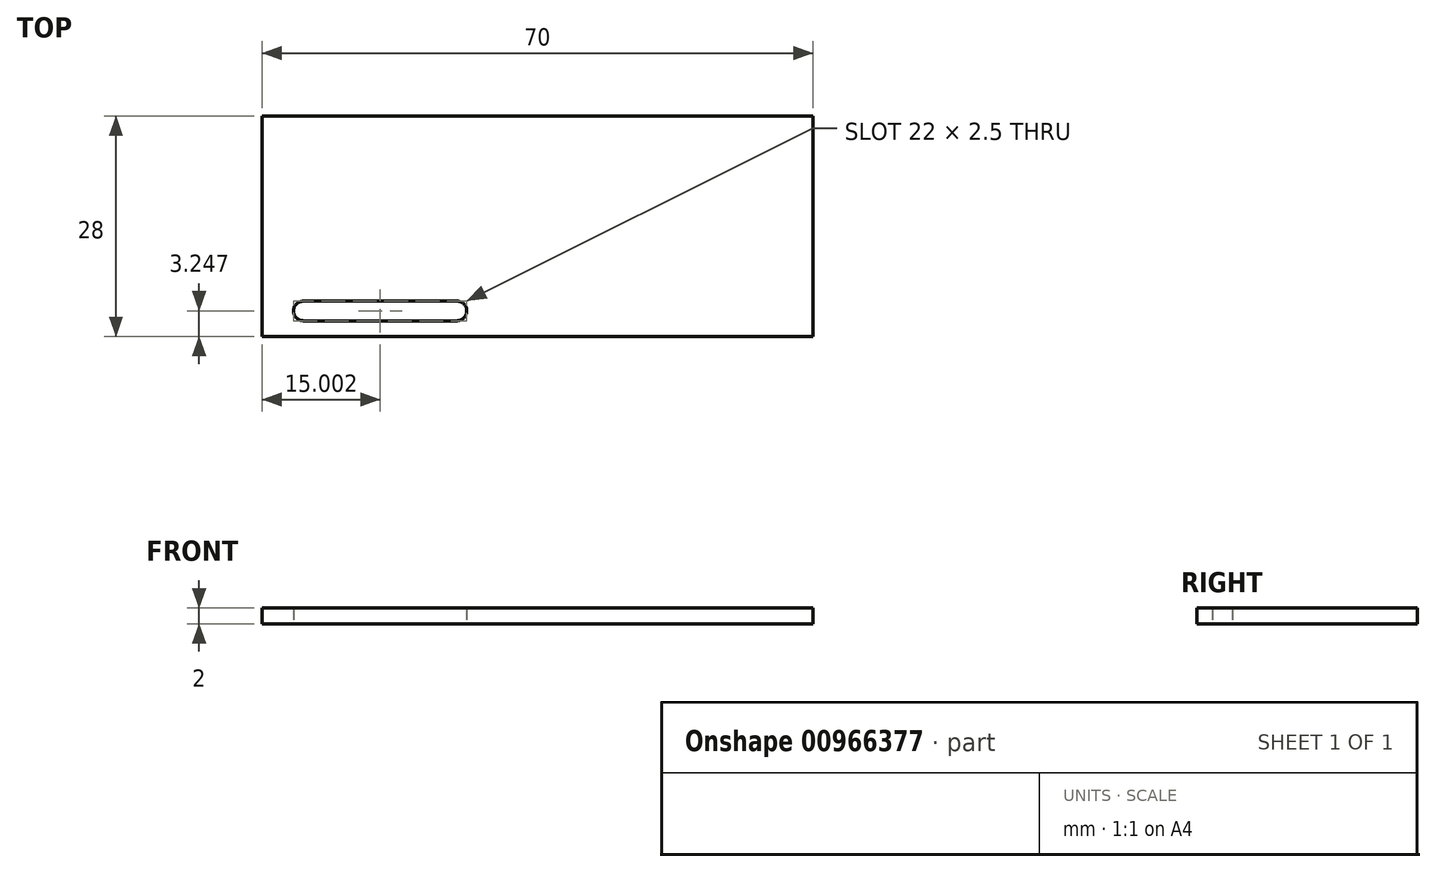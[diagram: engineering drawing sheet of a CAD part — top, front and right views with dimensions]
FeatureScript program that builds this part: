
annotation { "Feature Type Name" : "Feature", "Feature Type Description" : "" }
export const myFeature = defineFeature(function(context is Context, id is Id, definition is map)
    precondition{}
    {
        {
            var Q0;
            Q0=qCreatedBy(makeId("Top.planeOp"),FACE);
            var sketch = newSketch(context, id + "F0", { "sketchPlane" : qUnion([Q0])});
            skLineSegment(sketch, "E0.bottom", {"start": v(-29.62, 6.19) * mm, "end": v(40.38, 6.19) * mm});
            skLineSegment(sketch, "E0.top", {"start": v(-29.62, -21.81) * mm, "end": v(40.38, -21.81) * mm});
            skLineSegment(sketch, "E0.left", {"start": v(-29.62, 6.19) * mm, "end": v(-29.62, -21.81) * mm});
            skLineSegment(sketch, "E0.right", {"start": v(40.38, 6.19) * mm, "end": v(40.38, -21.81) * mm});
            skArc(sketch, "E1", {"start": v(-24.37, -17.31) * mm, "mid": v(-25.62, -18.56) * mm, "end": v(-24.37, -19.81) * mm});
            skArc(sketch, "E2", {"start": v(-4.87, -19.81) * mm, "mid": v(-3.62, -18.56) * mm, "end": v(-4.87, -17.31) * mm});
            skLineSegment(sketch, "E3", {"start": v(-24.37, -17.31) * mm, "end": v(-4.87, -17.31) * mm});
            skLineSegment(sketch, "E4", {"start": v(-24.37, -19.81) * mm, "end": v(-4.87, -19.81) * mm});
            skSolve(sketch);
        }
        {
            var Q0;
            Q0 = qSketchRegion(id + "F0", true);
            extrude(context, id + "F1", {"entities" : qUnion([Q0]), "depth" : 2 * mm, "offsetDistance" : 25 * mm});
        }
    });
